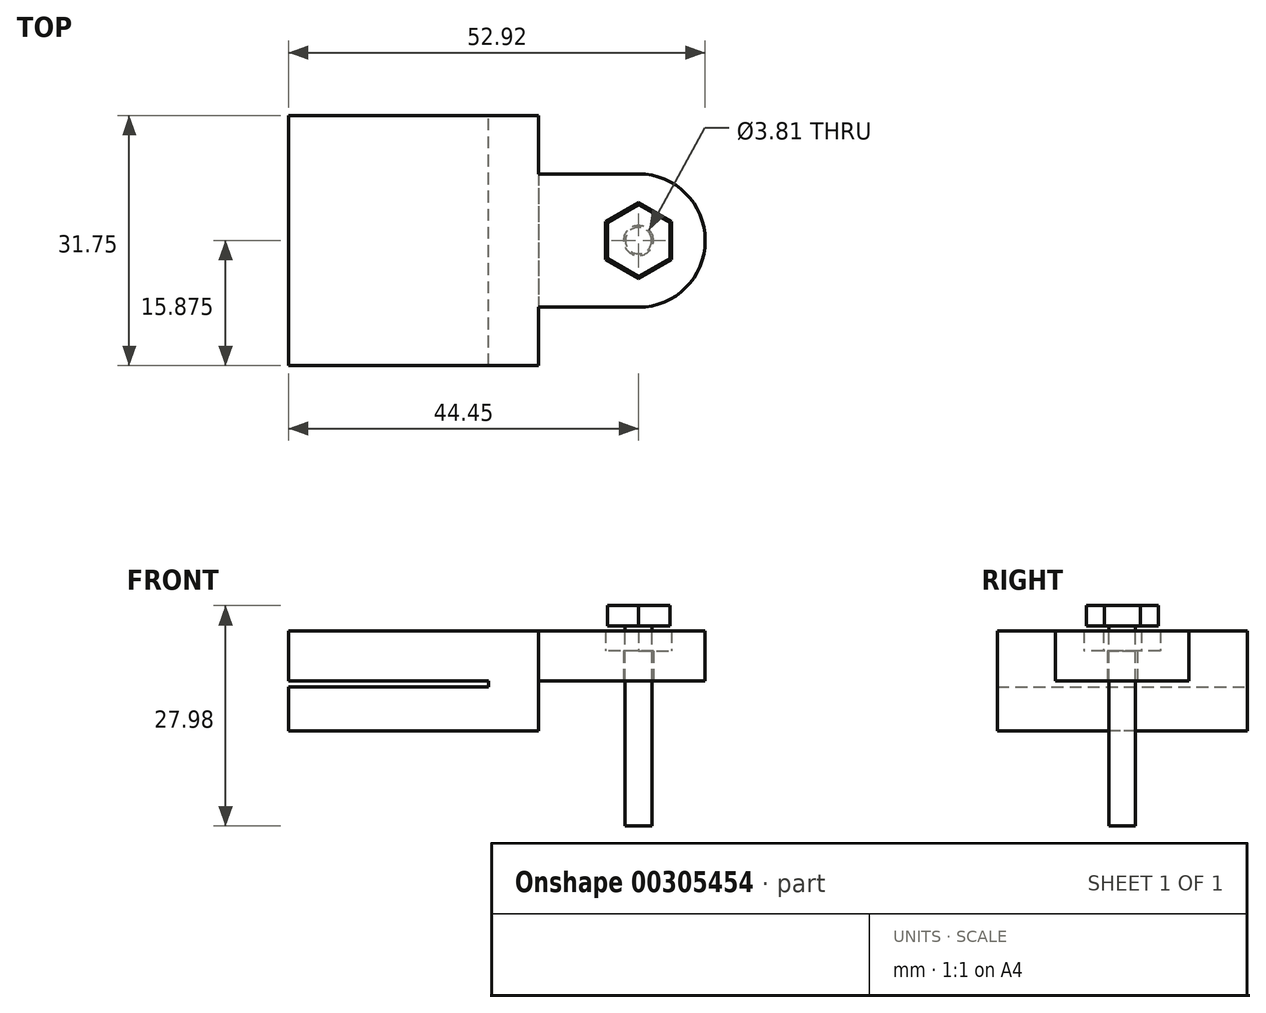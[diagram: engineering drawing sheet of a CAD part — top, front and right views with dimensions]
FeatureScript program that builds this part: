
annotation { "Feature Type Name" : "Feature", "Feature Type Description" : "" }
export const myFeature = defineFeature(function(context is Context, id is Id, definition is map)
    precondition{}
    {
        {
            var Q0;
            Q0=qCreatedBy(makeId("Top.planeOp"),FACE);
            var sketch = newSketch(context, id + "F0", { "sketchPlane" : qUnion([Q0])});
            skLineSegment(sketch, "E0.bottom", {"start": v(0, 31.75) * mm, "end": v(31.75, 31.75) * mm});
            skLineSegment(sketch, "E0.top", {"start": v(0, 0) * mm, "end": v(31.75, 0) * mm});
            skLineSegment(sketch, "E0.left", {"start": v(0, 31.75) * mm, "end": v(0, 0) * mm});
            skLineSegment(sketch, "E0.right", {"start": v(31.75, 31.75) * mm, "end": v(31.75, 0) * mm});
            skLineSegment(sketch, "E1.bottom", {"start": v(31.75, 24.34) * mm, "end": v(44.45, 24.34) * mm});
            skLineSegment(sketch, "E1.top", {"start": v(31.75, 7.4) * mm, "end": v(44.45, 7.4) * mm});
            skLineSegment(sketch, "E1.right", {"start": v(44.45, 24.34) * mm, "end": v(44.45, 7.4) * mm, "construction": true});
            skArc(sketch, "E2", {"start": v(44.45, 7.4) * mm, "mid": v(52.92, 15.87) * mm, "end": v(44.45, 24.34) * mm});
            skCircle(sketch, "E3", {"center": v(44.45, 15.87) * mm, "radius": 1.9 * mm});
            skCircle(sketch, "E4.cCircle", {"center": v(44.45, 15.87) * mm, "radius": 4.2 * mm, "construction": true});
            skLineSegment(sketch, "E4.0", {"start": v(48.64, 18.3) * mm, "end": v(48.64, 13.46) * mm});
            skLineSegment(sketch, "E4.1", {"start": v(48.64, 13.46) * mm, "end": v(44.45, 11.04) * mm});
            skLineSegment(sketch, "E4.2", {"start": v(44.45, 11.04) * mm, "end": v(40.26, 13.46) * mm});
            skLineSegment(sketch, "E4.3", {"start": v(40.26, 13.46) * mm, "end": v(40.26, 18.3) * mm});
            skLineSegment(sketch, "E4.4", {"start": v(40.26, 18.3) * mm, "end": v(44.45, 20.71) * mm});
            skLineSegment(sketch, "E4.5", {"start": v(44.45, 20.71) * mm, "end": v(48.64, 18.3) * mm});
            skPoint(sketch, "E4.0.midPoint", {"position": v(48.64, 15.87) * mm});
            skLineSegment(sketch, "E5", {"start": v(44.45, 15.88) * mm, "end": v(31.75, 15.88) * mm, "construction": true});
            skPoint(sketch, "E5.endSnap0", {"position": v(31.75, 15.88) * mm});
            skSolve(sketch);
        }
        {
            var Q0;
            {var subQ1=sQuery(id+"F0.wireOp",EDGE,"E0.bottom");Q0=makeQuery(id+"F0.imprint","IMPRINT",FACE,{"disambiguationData":[TD([[makeQuery(id+"F0.imprint","IMPRINT",EDGE,{"derivedFrom":subQ1}),-1.0]])]});}
            extrude(context, id + "F1", {"entities" : qUnion([Q0]), "endBound" : BoundingType.SYMMETRIC, "depth" : 12.7 * mm});
        }
        {
            var Q0;
            {var subQ0=sQuery(id+"F0.wireOp",EDGE,"E1.bottom");Q0=makeQuery(id+"F0.imprint","IMPRINT",FACE,{"disambiguationData":[TD([[makeQuery(id+"F0.imprint","IMPRINT",EDGE,{"derivedFrom":subQ0}),-1.0]])]});}
            var Q1;
            {var subQ0=sQuery(id+"F0.wireOp",EDGE,"E4.2");Q1=makeQuery(id+"F0.imprint","IMPRINT",FACE,{"disambiguationData":[TD([[makeQuery(id+"F0.imprint","IMPRINT",EDGE,{"derivedFrom":subQ0}),1.0]])]});}
            var Q2;
            Q2=makeQuery(id+"F0.imprint","IMPRINT",FACE,{"disambiguationData":[TD([[makeQuery(id+"F0.imprint","IMPRINT",EDGE,{"derivedFrom":sQuery(id+"F0.wireOp",EDGE,"E4.0")}),1.0]])]});
            extrude(context, id + "F2", {"entities" : qUnion([Q0, Q1, Q2]), "operationType" : NewBodyOperationType.ADD, "depth" : 6.35 * mm});
        }
        {
            var Q0;
            {var subQ4=sQuery(id+"F0.wireOp",EDGE,"E4.2");Q0=makeQuery(id+"F0.imprint","IMPRINT",FACE,{"disambiguationData":[TD([[makeQuery(id+"F0.imprint","IMPRINT",EDGE,{"derivedFrom":subQ4}),-1.0]])]});}
            var Q1;
            Q1=makeQuery(id+"F0.imprint","IMPRINT",FACE,{"disambiguationData":[TD([[makeQuery(id+"F0.imprint","IMPRINT",EDGE,{"derivedFrom":sQuery(id+"F0.wireOp",EDGE,"E4.0")}),-1.0]])]});
            extrude(context, id + "F3", {"entities" : qUnion([Q0, Q1]), "operationType" : NewBodyOperationType.ADD, "depth" : 3.8 * mm});
        }
        {
            var Q0;
            Q0=makeQuery(id+"F1.opExtrude","SWEPT_FACE",FACE,{"disambiguationData":[OSD([sQuery(id+"F0.wireOp",EDGE,"E0.bottom")])]});
            var sketch = newSketch(context, id + "F4", { "sketchPlane" : qUnion([Q0])});
            skLineSegment(sketch, "E6.bottom", {"start": v(0, 0) * mm, "end": v(-25.4, 0) * mm});
            skLineSegment(sketch, "E6.top", {"start": v(0, -0.8) * mm, "end": v(-25.4, -0.8) * mm});
            skLineSegment(sketch, "E6.left", {"start": v(0, 0) * mm, "end": v(0, -0.8) * mm});
            skLineSegment(sketch, "E6.right", {"start": v(-25.4, 0) * mm, "end": v(-25.4, -0.8) * mm});
            skLineSegment(sketch, "E7.bottom", {"start": v(-25.4, 0) * mm, "end": v(0, 0) * mm});
            skLineSegment(sketch, "E7.top", {"start": v(-25.4, 0.8) * mm, "end": v(0, 0.8) * mm});
            skLineSegment(sketch, "E7.left", {"start": v(-25.4, 0) * mm, "end": v(-25.4, 0.8) * mm});
            skLineSegment(sketch, "E7.right", {"start": v(0, 0) * mm, "end": v(0, 0.8) * mm});
            skSolve(sketch);
        }
        {
            var Q0;
            Q0=makeQuery(id+"F4.imprint","IMPRINT",FACE,{"disambiguationData":[TD([[makeQuery(id+"F4.imprint","IMPRINT",EDGE,{"derivedFrom":sQuery(id+"F4.wireOp",EDGE,"E7.bottom")}),1.0]])]});
            var Q1;
            Q1=makeQuery(id+"F4.imprint","IMPRINT",FACE,{"disambiguationData":[TD([[makeQuery(id+"F4.imprint","IMPRINT",EDGE,{"derivedFrom":sQuery(id+"F4.wireOp",EDGE,"E6.top")}),-1.0]])]});
            extrude(context, id + "F5", {"entities" : qUnion([Q0, Q1]), "operationType" : NewBodyOperationType.REMOVE, "endBound" : BoundingType.THROUGH_ALL, "oppositeDirection" : true, "depth" : 25.4 * mm});
        }
        {
            var Q0;
            Q0=makeQuery(id+"F3.opExtrude","CAP_FACE",FACE,{"disambiguationData":[OSD([sQuery(id+"F0.wireOp",EDGE,"E3"),sQuery(id+"F0.wireOp",EDGE,"E4.0"),sQuery(id+"F0.wireOp",EDGE,"E4.1"),sQuery(id+"F0.wireOp",EDGE,"E4.2"),sQuery(id+"F0.wireOp",EDGE,"E4.3"),sQuery(id+"F0.wireOp",EDGE,"E4.4"),sQuery(id+"F0.wireOp",EDGE,"E4.5")])],"isStart":false});
            cPlane(context, id + "F6", {"entities" : qUnion([Q0]), "cplaneType" : CPlaneType.OFFSET, "offset" : 3.17 * mm, "width" : 152.4 * mm, "height" : 152.4 * mm});
        }
        {
            var Q0;
            Q0=qCreatedBy(id+"F6.planeOp",FACE);
            var sketch = newSketch(context, id + "F7", { "sketchPlane" : qUnion([Q0])});
            skCircle(sketch, "E8.cCircle", {"center": v(44.45, 15.88) * mm, "radius": 3.97 * mm, "construction": true});
            skLineSegment(sketch, "E8.0", {"start": v(48.42, 18.17) * mm, "end": v(48.42, 13.58) * mm});
            skLineSegment(sketch, "E8.1", {"start": v(48.42, 13.58) * mm, "end": v(44.45, 11.3) * mm});
            skLineSegment(sketch, "E8.2", {"start": v(44.45, 11.3) * mm, "end": v(40.48, 13.58) * mm});
            skLineSegment(sketch, "E8.3", {"start": v(40.48, 13.58) * mm, "end": v(40.48, 18.17) * mm});
            skLineSegment(sketch, "E8.4", {"start": v(40.48, 18.17) * mm, "end": v(44.45, 20.46) * mm});
            skLineSegment(sketch, "E8.5", {"start": v(44.45, 20.46) * mm, "end": v(48.42, 18.17) * mm});
            skPoint(sketch, "E8.0.midPoint", {"position": v(48.42, 15.88) * mm});
            skCircle(sketch, "E9", {"center": v(44.45, 15.88) * mm, "radius": 1.69 * mm});
            skSolve(sketch);
        }
        {
            var Q0;
            Q0=makeQuery(id+"F7.imprint","IMPRINT",FACE,{"disambiguationData":[TD([[makeQuery(id+"F7.imprint","IMPRINT",EDGE,{"derivedFrom":sQuery(id+"F7.wireOp",EDGE,"E9")}),1.0]])]});
            extrude(context, id + "F8", {"entities" : qUnion([Q0]), "oppositeDirection" : true, "depth" : 25.4 * mm});
        }
        {
            var Q0;
            Q0 = qSketchRegion(id + "F7", true);
            var Q1;
            Q1=makeQuery(id+"F7.imprint","IMPRINT",FACE,{"disambiguationData":[TD([[makeQuery(id+"F7.imprint","IMPRINT",EDGE,{"derivedFrom":sQuery(id+"F7.wireOp",EDGE,"E9")}),1.0]])]});
            extrude(context, id + "F9", {"entities" : qUnion([Q0, Q1]), "operationType" : NewBodyOperationType.ADD, "depth" : 2.58 * mm});
        }
    });
